# Revit family: Domotics-DomesticRanges-GEWISS-CHORUS_POWER-SOCKET-OUTLET_ITA_P11P17_16A
name_source: partatom
category: Apparecchi elettrici
revit_build: Autodesk Revit 2016 (Build: 20161004_0715(x64)
units: mm (PartAtom-declared; Revit-internal decimal feet)

## family parameters
Condiviso = Sì
Host = Superficie
Mantenere orientamento annotazione = Sì
Numero OmniClass = 23.80.50.14
Punto di calcolo locali = Sì
Quota connettore circolare = Usa diametro
Taglio con vuoti quando caricato = Sì
Tipo di parte = Normale
Titolo OmniClass = Plug Connectors

## types (6) — shared parameters
Breaking capacity: = 1.25 In (100 position changes)
Carico apparente = 0 VA
Catalogue = DOMOTICS
Catalogue Range = CHORUS - DOMESTIC RANGE
Category = Dual amperage socket-outlet
Characteristics = With safety shields
Description. = Dual amperage socket-outlet
Description: = 2P+E - 16 A Dual amperage
Electrocod = 0131
For plug pins = Ã˜ 4 / 5 mm
Glow Wire Test = 850°C
IDF = e51a4de5-cedc-4b23-a4cc-bbf58c90be0d
IDT = 29c87b2e-b13e-4cda-8006-9f3203d1c943
Immagine tipo = GW14203.jpg
Insulation resistance = > 5 MOhm
Larghezza presa = 23 mm  [stored 0.0754593 ft]
N. poli = 1
No. Chorus modules = 1
No. Chorus modules: = 1
Produttore = GEWISS S.p.A.
Prolonged operation (no.of position changes) = 10.000 at In 250 V ac cosÃ˜=0,8
Prospetto di default = 1219 mm
Resistance at test voltage = 2000 V at 50 Hz for 1 minute
SEO = Socket outlet
Simbolo = SIMBOLO PRESE : PRESA
Socket-out type = P11-P17
Standard = English
Standard: = English
Standard; = IEC 60884-1
Technical sheet = https://www.gewiss.com
Terminal grip on cable traction = > 50 N
Terminal tightening capacity flexible cables (mm2) = min. 0,75 - max. 2x4
Terminal tightening capacity rigid cables (mm2) = min. 0,5 - max. 2x2,5
Thermo-pressure with ball = 125
Tipo = CHORUS PRESE ITA P11-17 16A_BASE : TITANIO
URL = https://www.gewiss.com
Version file RFA = 19.0
Volt = 230 V
Voltage = 250 V ac
Voltage: = 250 V ac
Wiring terminals = With screw

## per-type parameters (varying)
| type | Colour | Descrizione | EAN code | Modello | Type: |
| GW10203 - White | White | S. OUT. 1M 2P+E 16A D.AM P17-11 IT WH | 8011564257894 | GW10203 |  |
| GW10223 - Verde | Green | S. OUT. 1M 2P+E 16A D.AM P17-11 IT GREEN | 8011564264861 | GW10223 | For allocated lines |
| GW10233 - Arancio | Orange | S. OUT. 1M 2P+E 16A D.AM P17-11 IT ORAN | 8011564264878 | GW10233 | For allocated lines |
| GW14203 - Titanium | Titanium | SOCKET 1M 2P+E 16A D.AM P17-11 IT ST T | 8011564266308 | GW14203 |  |
| GW10213 - Rosso | Red | S. OUT. 1M 2P+E 16A D.AM P17-11 IT RED | 8011564264854 | GW10213 | For allocated lines |
| GW12203 - Black | Black | SOCKET, 1M 2P+E 16A D.AM P17-11 IT ST B | 8011564267312 | GW12203 |  |

note: source unit labels omitted for Thermo-pressure with ball — the stored unit's dimension contradicts the parameter name (converter mislabeling)

note: [stored X ft] marks values corroborated as IEEE doubles in the binary element streams (Revit-internal decimal feet)

## geometry (parser evidence)
native form markers: Sweep x2
no freeform markers — native parametric forms only
